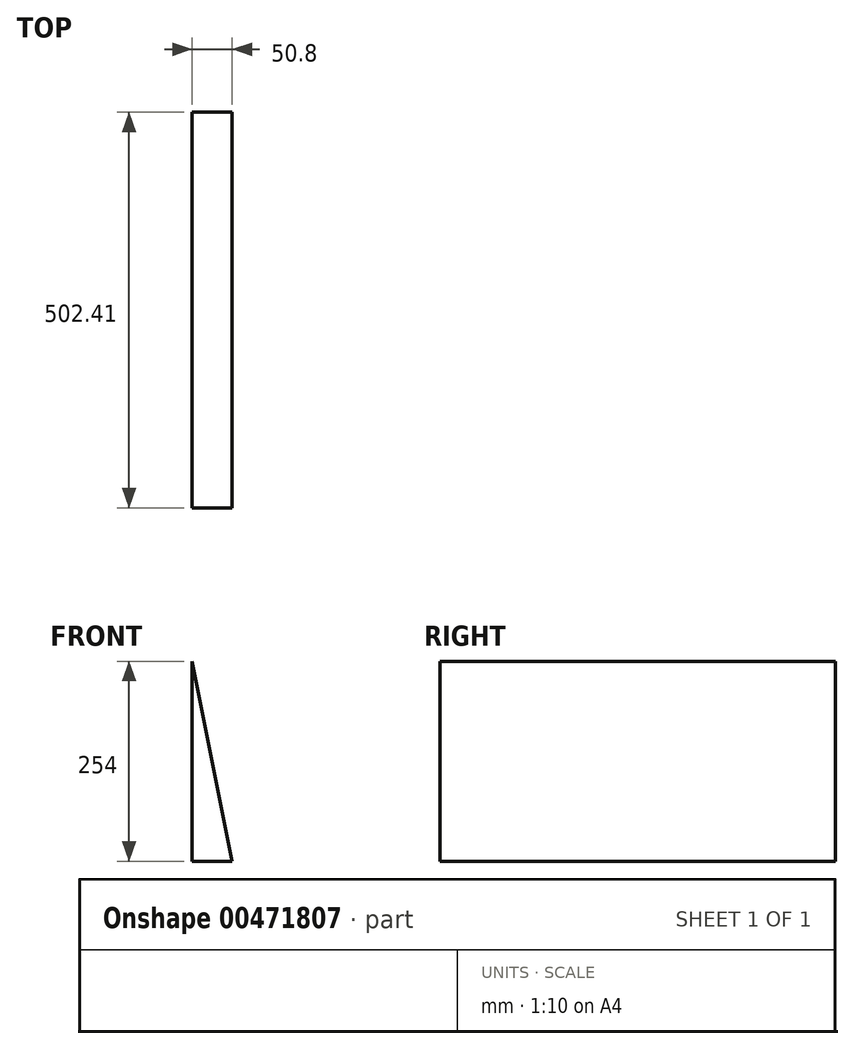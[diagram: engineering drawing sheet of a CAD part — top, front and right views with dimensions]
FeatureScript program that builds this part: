
annotation { "Feature Type Name" : "Feature", "Feature Type Description" : "" }
export const myFeature = defineFeature(function(context is Context, id is Id, definition is map)
    precondition{}
    {
        {
            var Q0;
            Q0=qCreatedBy(makeId("Front.planeOp"),FACE);
            var sketch = newSketch(context, id + "F0", { "sketchPlane" : qUnion([Q0])});
            skLineSegment(sketch, "E0", {"start": v(-76.2, 0) * mm, "end": v(-76.2, 254) * mm});
            skLineSegment(sketch, "E1", {"start": v(-76.2, 254) * mm, "end": v(-25.4, 0) * mm});
            skLineSegment(sketch, "E2", {"start": v(-25.4, 0) * mm, "end": v(-76.2, 0) * mm});
            skSolve(sketch);
        }
        {
            var Q0;
            Q0 = qSketchRegion(id + "F0", true);
            var Q1;
            Q1=makeQuery(id+"F0.imprint","IMPRINT",FACE,{"disambiguationData":[TD([[makeQuery(id+"F0.imprint","IMPRINT",EDGE,{"derivedFrom":sQuery(id+"F0.wireOp",EDGE,"E0")}),-1.0]])]});
            extrude(context, id + "F1", {"entities" : qUnion([Q0, Q1]), "oppositeDirection" : true, "depth" : 502.41 * mm});
        }
    });
